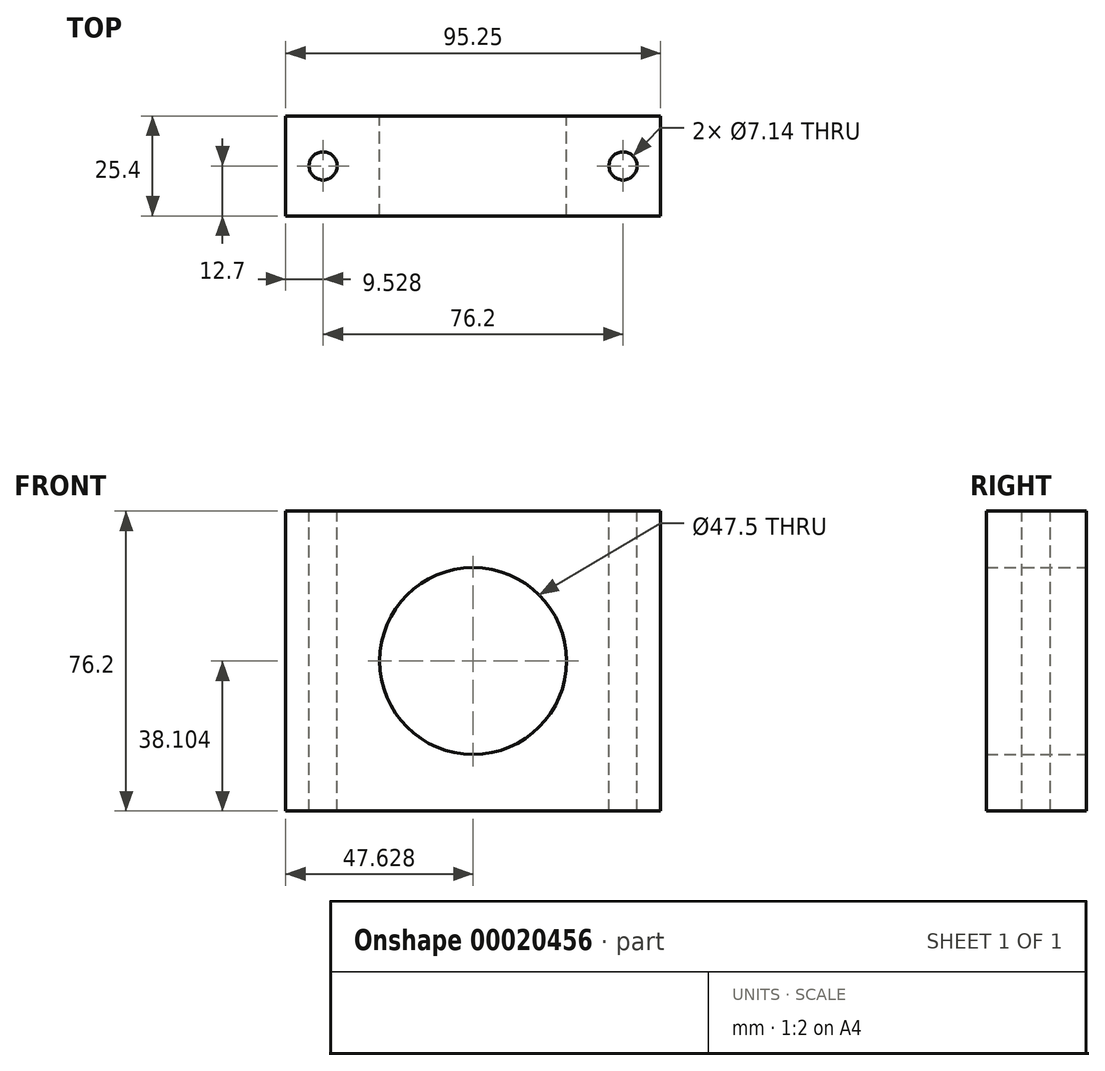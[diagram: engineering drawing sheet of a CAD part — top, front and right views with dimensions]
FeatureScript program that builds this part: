
annotation { "Feature Type Name" : "Feature", "Feature Type Description" : "" }
export const myFeature = defineFeature(function(context is Context, id is Id, definition is map)
    precondition{}
    {
        {
            var Q0;
            Q0=qCreatedBy(makeId("Front.planeOp"),FACE);
            var sketch = newSketch(context, id + "F0", { "sketchPlane" : qUnion([Q0])});
            skLineSegment(sketch, "E0.bottom", {"start": v(-56.34, 27.44) * mm, "end": v(38.91, 27.44) * mm});
            skLineSegment(sketch, "E0.top", {"start": v(-56.34, -48.76) * mm, "end": v(38.91, -48.76) * mm});
            skLineSegment(sketch, "E0.left", {"start": v(-56.34, 27.44) * mm, "end": v(-56.34, -48.76) * mm});
            skLineSegment(sketch, "E0.right", {"start": v(38.91, 27.44) * mm, "end": v(38.91, -48.76) * mm});
            skLineSegment(sketch, "E1.0", {"start": v(-8.84, 27.44) * mm, "end": v(-8.84, -48.76) * mm, "construction": true});
            skLineSegment(sketch, "E2.0", {"start": v(-56.34, -10.66) * mm, "end": v(38.91, -10.66) * mm, "construction": true});
            skCircle(sketch, "E3", {"center": v(-8.71, -10.66) * mm, "radius": 23.75 * mm});
            skSolve(sketch);
        }
        {
            var Q0;
            Q0 = qSketchRegion(id + "F0", true);
            extrude(context, id + "F1", {"entities" : qUnion([Q0]), "depth" : 25.4 * mm});
        }
        {
            var Q0;
            Q0=makeQuery(id+"F1.opExtrude","SWEPT_FACE",FACE,{"disambiguationData":[OSD([sQuery(id+"F0.wireOp",EDGE,"E0.bottom")])]});
            var sketch = newSketch(context, id + "F2", { "sketchPlane" : qUnion([Q0])});
            skLineSegment(sketch, "E4.0", {"start": v(29.39, -25.4) * mm, "end": v(29.39, 0) * mm, "construction": true});
            skLineSegment(sketch, "E5.0", {"start": v(-46.81, -25.4) * mm, "end": v(-46.81, 0) * mm, "construction": true});
            skLineSegment(sketch, "E6.0", {"start": v(-56.34, -12.7) * mm, "end": v(38.91, -12.7) * mm, "construction": true});
            skCircle(sketch, "E7", {"center": v(29.39, -12.7) * mm, "radius": 3.57 * mm});
            skCircle(sketch, "E8", {"center": v(-46.81, -12.7) * mm, "radius": 3.57 * mm});
            skSolve(sketch);
        }
        {
            var Q0;
            Q0 = qSketchRegion(id + "F2", true);
            extrude(context, id + "F3", {"entities" : qUnion([Q0]), "operationType" : NewBodyOperationType.REMOVE, "endBound" : BoundingType.THROUGH_ALL, "oppositeDirection" : true, "depth" : 25.4 * mm});
        }
        {
            var Q0;
            Q0 = qSketchRegion(id + "F2", true);
            extrude(context, id + "F4", {"entities" : qUnion([Q0]), "operationType" : NewBodyOperationType.REMOVE, "endBound" : BoundingType.THROUGH_ALL, "oppositeDirection" : true, "depth" : 25.4 * mm});
        }
    });
